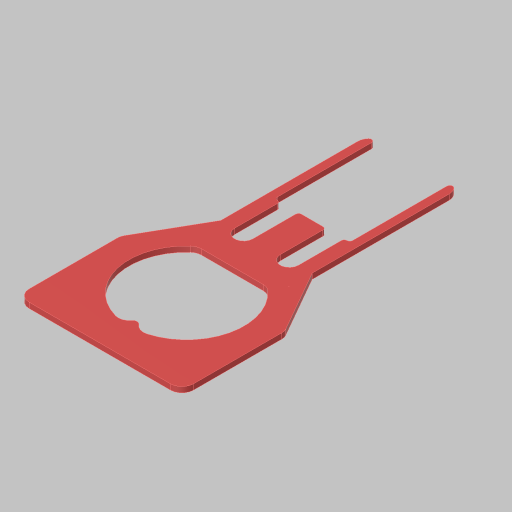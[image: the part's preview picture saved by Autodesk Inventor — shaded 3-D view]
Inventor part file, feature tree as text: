
AUTODESK INVENTOR PART (.ipt)
format: ipt  version: 2023.5 (Build 275446000, 446)  size: 312,320 bytes
history: native  units: in
note: dims shown in document units (in); Inventor stores cm internally (conversion verified against a paired STEP export)
features: extrude x8, sketch x7, fillet x5, projected_geometry x5
ambient origin geometry x8: Origin, YZ Plane, XZ Plane, XY Plane, X Axis, Y Axis, Z Axis, Center Point
bodies: Solid1 (feature_tree)
feature tree (25):
  sketch  "Sketch1"  dims[d1=0.7in d3=0.125in d4=0.197in]
  extrude  "Extrusion1"  Depth=0.125in
  fillet  "Fillet1"  Radius=0.197in
  extrude  "Extrusion2"  Depth=1.0in
  extrude  "Extrusion3"  Depth=0.5in
  fillet  "Fillet2"  Radius=0.5in
  extrude  "Extrusion4"  Depth=0.125in TaperAngle=0.0deg
  fillet  "Fillet3"  Radius=0.125in
  extrude  "Extrusion5"  Depth=0.5in
  fillet  "Fillet4"  Radius=1.375in
  extrude  "Extrusion7"  Depth=1.0in TaperAngle=0.0deg
  extrude  "Extrusion8"  Depth=0.5in
  fillet  "Fillet5"  Radius=0.125in
  extrude  "Extrusion9"  Depth=1.0in TaperAngle=0.0deg
  sketch  "Sketch2"  dims[d5=0.197in d8=1.0in]
  sketch  "Sketch3"  dims[d9=2.0in d10=0.25in d11=0.5in]
  sketch  "Sketch4"  dims[d12=0.25in d13=0.25in d14=0.0in d22=0.125in]
  sketch  "Sketch5"  dims[d23=0.201in d24=0.5in d26=1.375in]
  sketch  "Sketch7"  dims[d27=0.5in d28=1.0in d29=0.0in]
  sketch  "Sketch8"  dims[d30=1.26in d31=0.5in d32=0.125in d33=1.0in d34=0.0in d35=0.125in d36=0.093in d37=0.042in d38=1.0in d39=0.0in d40=0.125in d41=0.7874in d43=0.197in d44=0.3937in d46=1.0in d48=1.8in d49=3.45in d50=1.125in d51=1.0in d52=0.0in d53=0.125in d58=0.17in d59=0.0in d61=0.06in d62=0.0in d63=0.0312in d64=1.0in d65=0.0in]
  projected_geometry  "Project Cut Edges1"
  projected_geometry  "Project Cut Edges2"
  projected_geometry  "Project Cut Edges3"
  projected_geometry  "Project Cut Edges4"
  projected_geometry  "Project Cut Edges5"
